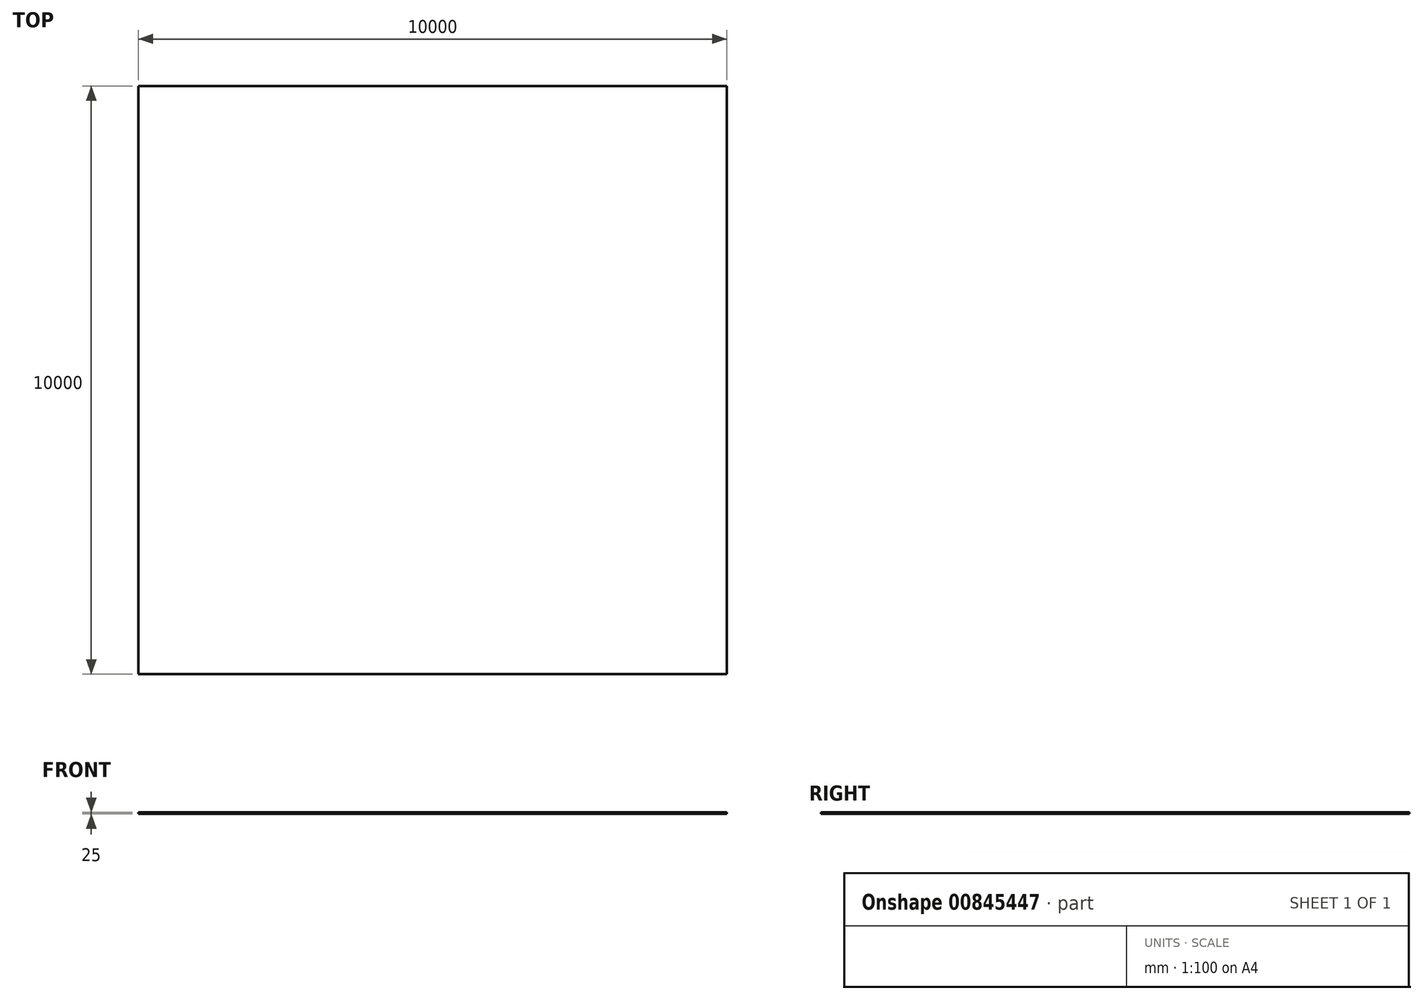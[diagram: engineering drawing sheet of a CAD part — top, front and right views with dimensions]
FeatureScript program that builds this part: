
annotation { "Feature Type Name" : "Feature", "Feature Type Description" : "" }
export const myFeature = defineFeature(function(context is Context, id is Id, definition is map)
    precondition{}
    {
        {
            var Q0;
            Q0=qCreatedBy(makeId("Top.planeOp"),FACE);
            var sketch = newSketch(context, id + "F0", { "sketchPlane" : qUnion([Q0])});
            skLineSegment(sketch, "E0.bottom", {"start": v(-878.23, 9948) * mm, "end": v(9121.77, 9948) * mm});
            skLineSegment(sketch, "E0.top", {"start": v(-878.23, -52) * mm, "end": v(9121.77, -52) * mm});
            skLineSegment(sketch, "E0.left", {"start": v(-878.23, 9948) * mm, "end": v(-878.23, -52) * mm});
            skLineSegment(sketch, "E0.right", {"start": v(9121.77, 9948) * mm, "end": v(9121.77, -52) * mm});
            skSolve(sketch);
        }
        {
            var Q0;
            Q0=makeQuery(id+"F0.imprint","IMPRINT",FACE,{"disambiguationData":[TD([[makeQuery(id+"F0.imprint","IMPRINT",EDGE,{"derivedFrom":sQuery(id+"F0.wireOp",EDGE,"E0.bottom")}),-1.0]])]});
            extrude(context, id + "F1", {"entities" : qUnion([Q0]), "depth" : 25 * mm, "offsetDistance" : 25 * mm});
        }
    });
